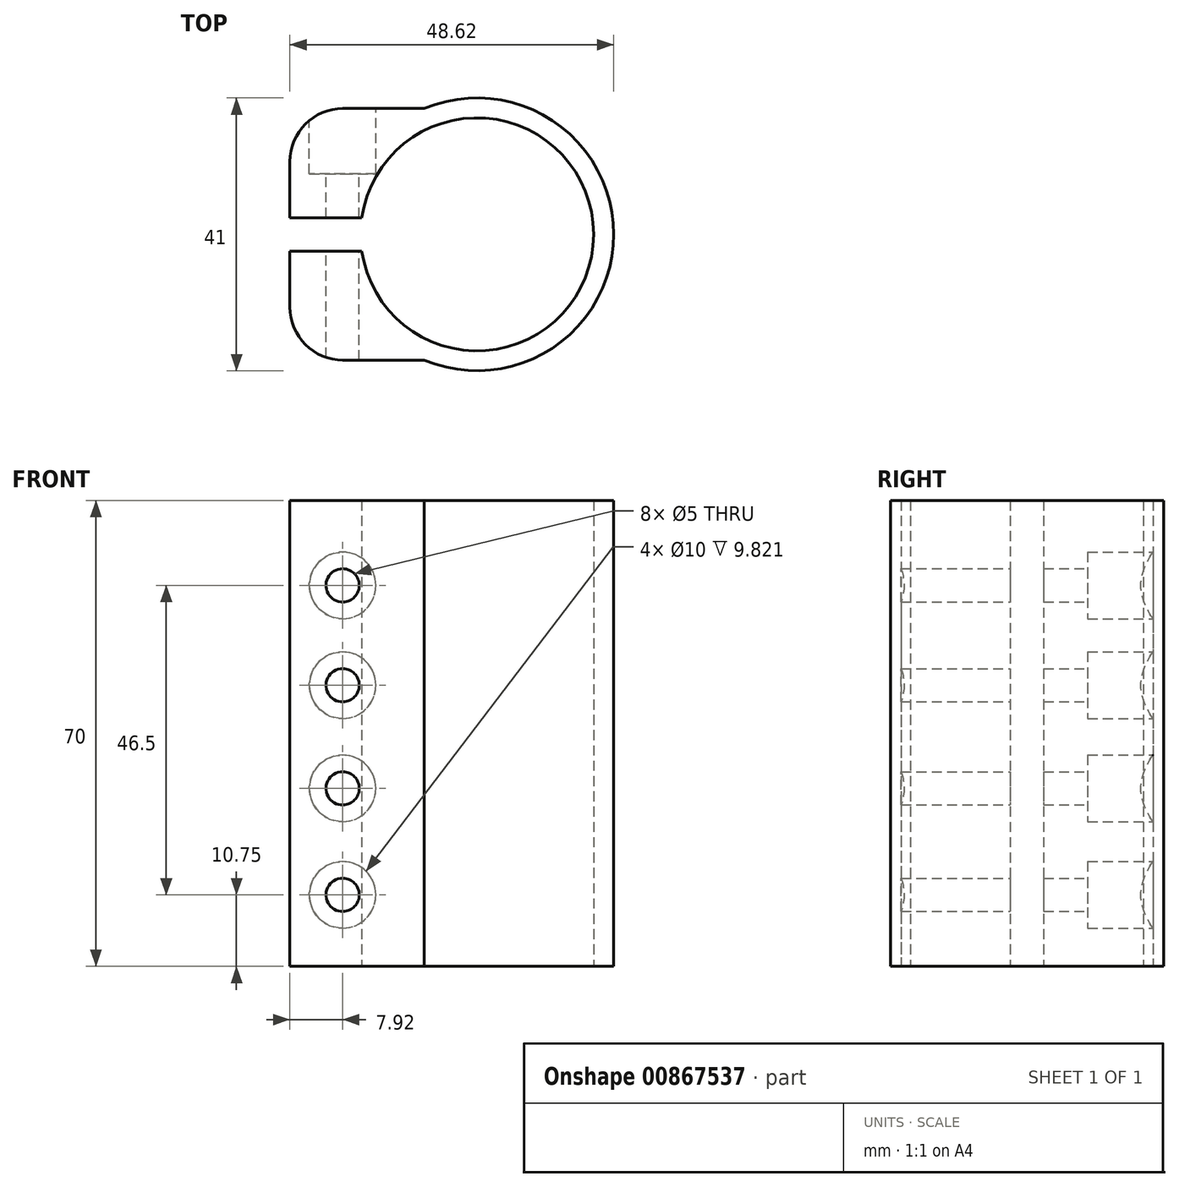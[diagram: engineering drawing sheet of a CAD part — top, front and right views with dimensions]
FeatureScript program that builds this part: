
annotation { "Feature Type Name" : "Feature", "Feature Type Description" : "" }
export const myFeature = defineFeature(function(context is Context, id is Id, definition is map)
    precondition{}
    {
        {
            var Q0;
            Q0=qCreatedBy(makeId("Top.planeOp"),FACE);
            var sketch = newSketch(context, id + "F0", { "sketchPlane" : qUnion([Q0])});
            skArc(sketch, "E0", {"start": v(-17.32, -2.5) * mm, "mid": v(17.5, 0) * mm, "end": v(-17.32, 2.5) * mm});
            skArc(sketch, "E1", {"start": v(-7.92, -18.9) * mm, "mid": v(20.5, 0) * mm, "end": v(-7.92, 18.9) * mm});
            skLineSegment(sketch, "E2", {"start": v(-7.92, 18.9) * mm, "end": v(-20.12, 18.9) * mm});
            skLineSegment(sketch, "E3", {"start": v(-28.12, 10.9) * mm, "end": v(-28.12, 2.5) * mm});
            skLineSegment(sketch, "E4", {"start": v(-28.12, 2.5) * mm, "end": v(-17.32, 2.5) * mm});
            skPoint(sketch, "E5.visualSharp", {"position": v(-28.12, 18.9) * mm});
            skArc(sketch, "E5.filletArc", {"start": v(-20.12, 18.9) * mm, "mid": v(-25.78, 16.57) * mm, "end": v(-28.12, 10.9) * mm});
            skLineSegment(sketch, "E6", {"start": v(0, 0) * mm, "end": v(31.32, 0) * mm, "construction": true});
            skLineSegment(sketch, "E7.MirrorCS", {"start": v(-7.92, -18.9) * mm, "end": v(-20.12, -18.9) * mm});
            skArc(sketch, "E8.MirrorCS", {"start": v(-20.12, -18.9) * mm, "mid": v(-25.78, -16.57) * mm, "end": v(-28.12, -10.9) * mm});
            skLineSegment(sketch, "E9.MirrorCS", {"start": v(-28.12, -10.9) * mm, "end": v(-28.12, -2.5) * mm});
            skLineSegment(sketch, "E10.MirrorCS", {"start": v(-28.12, -2.5) * mm, "end": v(-17.32, -2.5) * mm});
            skSolve(sketch);
        }
        {
            var Q0;
            Q0=makeQuery(id+"F0.imprint","IMPRINT",FACE,{"disambiguationData":[TD([[makeQuery(id+"F0.imprint","IMPRINT",EDGE,{"derivedFrom":sQuery(id+"F0.wireOp",EDGE,"E0")}),-1.0]])]});
            extrude(context, id + "F1", {"entities" : qUnion([Q0]), "endBound" : BoundingType.SYMMETRIC, "depth" : 70 * mm, "offsetDistance" : 25 * mm});
        }
        {
            var Q0;
            Q0=makeQuery(id+"F1.opExtrude","SWEPT_FACE",FACE,{"disambiguationData":[OSD([sQuery(id+"F0.wireOp",EDGE,"E2")])]});
            var sketch = newSketch(context, id + "F2", { "sketchPlane" : qUnion([Q0])});
            skPoint(sketch, "E11", {"position": v(20.2, -24.25) * mm});
            skPoint(sketch, "E12", {"position": v(20.2, -8.25) * mm});
            skPoint(sketch, "E13", {"position": v(20.2, 7.25) * mm});
            skPoint(sketch, "E14", {"position": v(20.2, 22.25) * mm});
            skSolve(sketch);
        }
        {
            var Q0;
            Q0=sQuery(id+"F2.wireOp",VERTEX,"E14");
            var Q1;
            Q1=sQuery(id+"F2.wireOp",VERTEX,"E13");
            var Q2;
            Q2=sQuery(id+"F2.wireOp",VERTEX,"E12");
            var Q3;
            Q3=sQuery(id+"F2.wireOp",VERTEX,"E11");
            var Q4;
            Q4=makeQuery(id+"F1.opExtrude","SWEPT_BODY",BODY,{"disambiguationData":[OSD([sQuery(id+"F0.wireOp",EDGE,"E0"),sQuery(id+"F0.wireOp",EDGE,"E1"),sQuery(id+"F0.wireOp",EDGE,"E2"),sQuery(id+"F0.wireOp",EDGE,"E3"),sQuery(id+"F0.wireOp",EDGE,"E4"),sQuery(id+"F0.wireOp",EDGE,"E5.filletArc"),sQuery(id+"F0.wireOp",EDGE,"E7.MirrorCS"),sQuery(id+"F0.wireOp",EDGE,"E8.MirrorCS"),sQuery(id+"F0.wireOp",EDGE,"E9.MirrorCS"),sQuery(id+"F0.wireOp",EDGE,"E10.MirrorCS")])]});
            hole(context, id + "F3", {"style" : HoleStyle.C_BORE, "endStyle" : HoleEndStyle.THROUGH, "holeDiameter" : 5 * mm, "cBoreDiameter" : 10 * mm, "cBoreDepth" : 8 * mm, "majorDiameter" : 5 * mm, "isTappedThrough" : true, "tappedDepth" : 12 * mm, "tapClearance" : 3, "locations" : qUnion([Q0, Q1, Q2, Q3]), "scope" : qUnion([Q4])});
        }
    });
